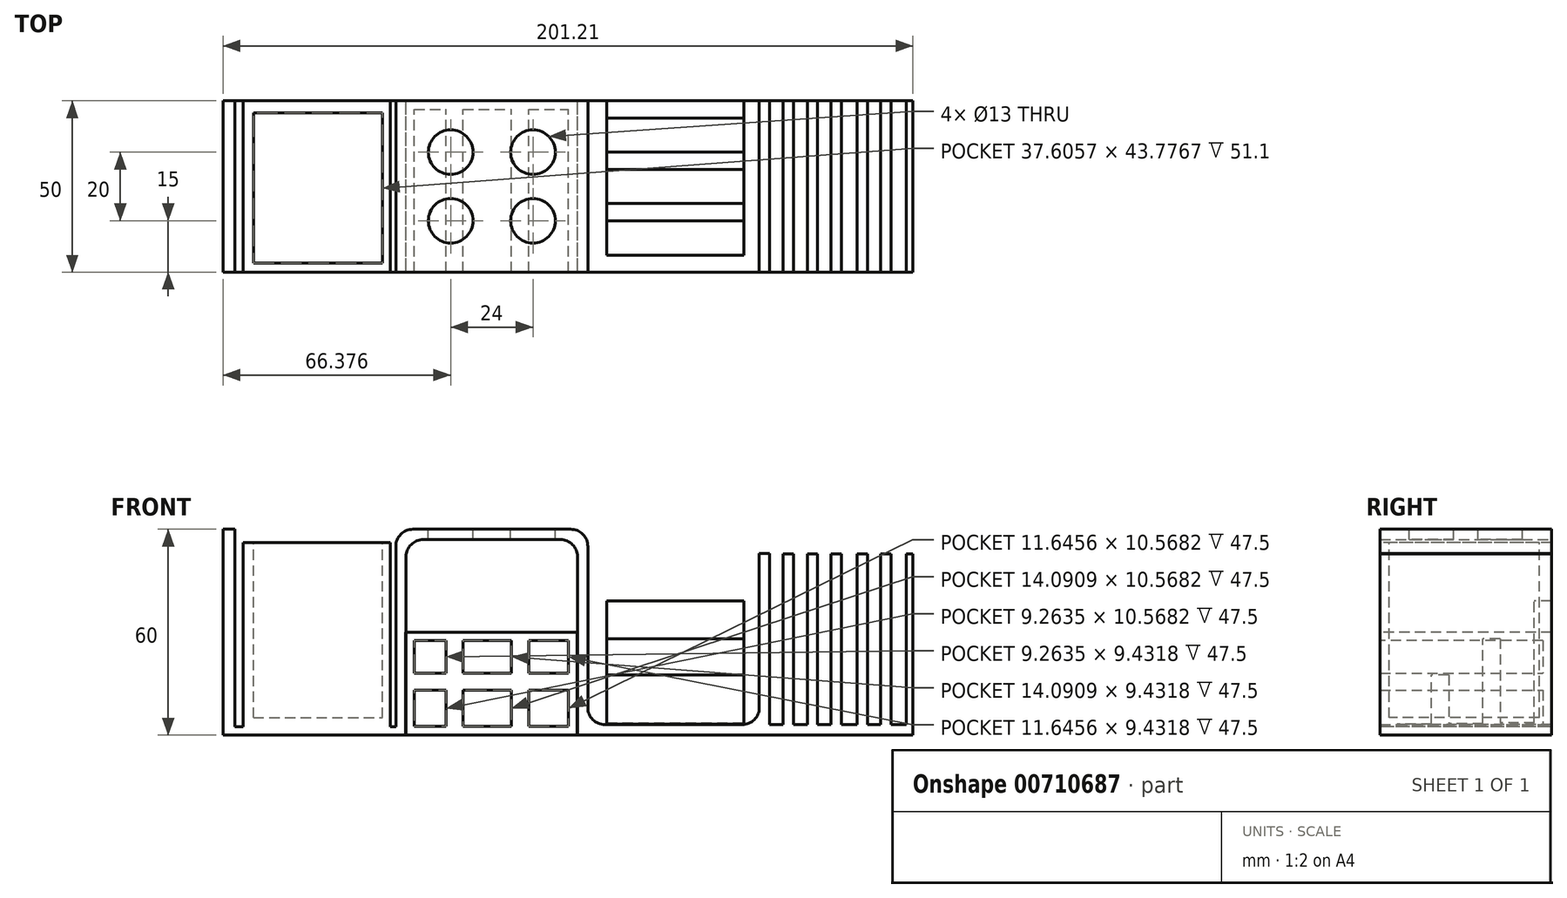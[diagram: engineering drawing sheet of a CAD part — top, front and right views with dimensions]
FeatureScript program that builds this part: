
annotation { "Feature Type Name" : "Feature", "Feature Type Description" : "" }
export const myFeature = defineFeature(function(context is Context, id is Id, definition is map)
    precondition{}
    {
        {
            var Q0;
            Q0=qCreatedBy(makeId("Front.planeOp"),FACE);
            var sketch = newSketch(context, id + "F0", { "sketchPlane" : qUnion([Q0])});
            skLineSegment(sketch, "E0.top", {"start": v(4.58, 57) * mm, "end": v(54.58, 57) * mm});
            skLineSegment(sketch, "E0.left", {"start": v(4.58, 0) * mm, "end": v(4.58, 57) * mm});
            skLineSegment(sketch, "E0.right", {"start": v(54.58, 0) * mm, "end": v(54.58, 57) * mm});
            skLineSegment(sketch, "E1.top", {"start": v(57.58, 3) * mm, "end": v(107.58, 3) * mm});
            skLineSegment(sketch, "E1.left", {"start": v(57.58, 60) * mm, "end": v(57.58, 3) * mm});
            skLineSegment(sketch, "E1.right", {"start": v(107.58, 53) * mm, "end": v(107.58, 3) * mm});
            skLineSegment(sketch, "E2", {"start": v(1.58, 0) * mm, "end": v(4.58, 0) * mm});
            skLineSegment(sketch, "E3", {"start": v(54.58, 0) * mm, "end": v(110.58, 0) * mm});
            skLineSegment(sketch, "E4", {"start": v(1.58, 60) * mm, "end": v(57.58, 60) * mm});
            skLineSegment(sketch, "E5", {"start": v(110.58, 53) * mm, "end": v(107.58, 53) * mm});
            skLineSegment(sketch, "E6.bottom", {"start": v(1.58, 0) * mm, "end": v(-45.36, 0) * mm});
            skLineSegment(sketch, "E6.top", {"start": v(1.58, 2.45) * mm, "end": v(-45.36, 2.45) * mm});
            skLineSegment(sketch, "E7.bottom", {"start": v(-45.36, 0) * mm, "end": v(-48.8, 0) * mm});
            skLineSegment(sketch, "E7.top", {"start": v(-45.36, 60) * mm, "end": v(-48.8, 60) * mm});
            skLineSegment(sketch, "E7.right", {"start": v(-48.8, 0) * mm, "end": v(-48.8, 60) * mm});
            skLineSegment(sketch, "E8", {"start": v(-45.36, 60) * mm, "end": v(-45.36, 2.45) * mm});
            skLineSegment(sketch, "E9", {"start": v(1.58, 60) * mm, "end": v(1.58, 2.45) * mm});
            skLineSegment(sketch, "E10.bottom", {"start": v(110.58, 0) * mm, "end": v(152.41, 0) * mm});
            skLineSegment(sketch, "E10.top", {"start": v(110.58, 3.01) * mm, "end": v(152.41, 3.01) * mm});
            skLineSegment(sketch, "E10.right", {"start": v(152.41, 0) * mm, "end": v(152.41, 3.01) * mm});
            skLineSegment(sketch, "E11", {"start": v(110.58, 53) * mm, "end": v(110.58, 3.01) * mm});
            skLineSegment(sketch, "E12.bottom", {"start": v(114.5, 3.01) * mm, "end": v(117.5, 3.01) * mm});
            skLineSegment(sketch, "E12.top", {"start": v(114.5, 52.83) * mm, "end": v(117.5, 52.83) * mm});
            skLineSegment(sketch, "E12.left", {"start": v(114.5, 3.01) * mm, "end": v(114.5, 52.83) * mm});
            skLineSegment(sketch, "E12.right", {"start": v(117.5, 3.01) * mm, "end": v(117.5, 52.83) * mm});
            skLineSegment(sketch, "E13.bottom", {"start": v(121.6, 3.01) * mm, "end": v(124.6, 3.01) * mm});
            skLineSegment(sketch, "E13.top", {"start": v(121.6, 52.83) * mm, "end": v(124.6, 52.83) * mm});
            skLineSegment(sketch, "E13.left", {"start": v(121.6, 3.01) * mm, "end": v(121.6, 52.83) * mm});
            skLineSegment(sketch, "E13.right", {"start": v(124.6, 3.01) * mm, "end": v(124.6, 52.83) * mm});
            skLineSegment(sketch, "E14.bottom", {"start": v(128.48, 3.01) * mm, "end": v(131.48, 3.01) * mm});
            skLineSegment(sketch, "E14.top", {"start": v(128.48, 52.83) * mm, "end": v(131.48, 52.83) * mm});
            skLineSegment(sketch, "E14.left", {"start": v(128.48, 3.01) * mm, "end": v(128.48, 52.83) * mm});
            skLineSegment(sketch, "E14.right", {"start": v(131.48, 3.01) * mm, "end": v(131.48, 52.83) * mm});
            skLineSegment(sketch, "E15.bottom", {"start": v(136.1, 3.01) * mm, "end": v(139.1, 3.01) * mm});
            skLineSegment(sketch, "E15.top", {"start": v(136.1, 52.83) * mm, "end": v(139.1, 52.83) * mm});
            skLineSegment(sketch, "E15.left", {"start": v(136.1, 3.01) * mm, "end": v(136.1, 52.83) * mm});
            skLineSegment(sketch, "E15.right", {"start": v(139.1, 3.01) * mm, "end": v(139.1, 52.83) * mm});
            skLineSegment(sketch, "E16.bottom", {"start": v(142.98, 3.01) * mm, "end": v(145.98, 3.01) * mm});
            skLineSegment(sketch, "E16.top", {"start": v(142.98, 52.83) * mm, "end": v(145.98, 52.83) * mm});
            skLineSegment(sketch, "E16.left", {"start": v(142.98, 3.01) * mm, "end": v(142.98, 52.83) * mm});
            skLineSegment(sketch, "E16.right", {"start": v(145.98, 3.01) * mm, "end": v(145.98, 52.83) * mm});
            skLineSegment(sketch, "E17.bottom", {"start": v(152.41, 3.01) * mm, "end": v(150.41, 3.01) * mm});
            skLineSegment(sketch, "E17.top", {"start": v(152.41, 52.83) * mm, "end": v(150.41, 52.83) * mm});
            skLineSegment(sketch, "E17.left", {"start": v(152.41, 3.01) * mm, "end": v(152.41, 52.83) * mm});
            skLineSegment(sketch, "E17.right", {"start": v(150.41, 3.01) * mm, "end": v(150.41, 52.83) * mm});
            skLineSegment(sketch, "E18", {"start": v(107.58, 3) * mm, "end": v(107.58, 0) * mm});
            skSolve(sketch);
        }
        {
            var Q0;
            Q0=qSketchRegion(id+"F0",true);
            extrude(context, id + "F1", {"entities" : qUnion([Q0]), "depth" : 50 * mm, "offsetDistance" : 25 * mm});
        }
        {
            var Q0;
            Q0=makeQuery(id+"F1.opExtrude","SWEPT_FACE",FACE,{"disambiguationData":[OSD([sQuery(id+"F0.wireOp",EDGE,"E4")])]});
            var sketch = newSketch(context, id + "F2", { "sketchPlane" : qUnion([Q0])});
            skCircle(sketch, "E19", {"center": v(17.58, -15) * mm, "radius": 6.5 * mm});
            skCircle(sketch, "E20", {"center": v(41.58, -15) * mm, "radius": 6.5 * mm});
            skCircle(sketch, "E21", {"center": v(17.58, -35) * mm, "radius": 6.5 * mm});
            skCircle(sketch, "E22", {"center": v(41.58, -35) * mm, "radius": 6.5 * mm});
            skSolve(sketch);
        }
        {
            var Q0;
            Q0=qCreatedBy(makeId("Top.planeOp"),FACE);
            var sketch = newSketch(context, id + "F3", { "sketchPlane" : qUnion([Q0])});
            skLineSegment(sketch, "E23.bottom", {"start": v(4.44, 0) * mm, "end": v(54.44, 0) * mm});
            skLineSegment(sketch, "E23.top", {"start": v(4.44, -50) * mm, "end": v(54.44, -50) * mm});
            skLineSegment(sketch, "E23.left", {"start": v(4.44, 0) * mm, "end": v(4.44, -50) * mm});
            skLineSegment(sketch, "E23.right", {"start": v(54.44, 0) * mm, "end": v(54.44, -50) * mm});
            skSolve(sketch);
        }
        {
            var Q0;
            Q0=makeQuery(id+"F1.opExtrude","SWEPT_FACE",FACE,{"disambiguationData":[OSD([sQuery(id+"F0.wireOp",EDGE,"E1.top")])]});
            var sketch = newSketch(context, id + "F4", { "sketchPlane" : qUnion([Q0])});
            skLineSegment(sketch, "E24.bottom", {"start": v(63.1, 0) * mm, "end": v(103.1, 0) * mm});
            skLineSegment(sketch, "E24.top", {"start": v(63.1, -15) * mm, "end": v(103.1, -15) * mm});
            skLineSegment(sketch, "E24.left", {"start": v(63.1, 0) * mm, "end": v(63.1, -15) * mm});
            skLineSegment(sketch, "E24.right", {"start": v(103.1, 0) * mm, "end": v(103.1, -15) * mm});
            skSolve(sketch);
        }
        {
            var Q0;
            Q0=qSketchRegion(id+"F4",true);
            extrude(context, id + "F5", {"entities" : qUnion([Q0]), "operationType" : NewBodyOperationType.ADD, "depth" : 36.1 * mm});
        }
        {
            var Q0;
            Q0=makeQuery(id+"F5.opExtrude","CAP_FACE",FACE,{"disambiguationData":[OSD([sQuery(id+"F4.wireOp",EDGE,"E24.bottom"),sQuery(id+"F4.wireOp",EDGE,"E24.top"),sQuery(id+"F4.wireOp",EDGE,"E24.left"),sQuery(id+"F4.wireOp",EDGE,"E24.right")])],"isStart":false});
            var sketch = newSketch(context, id + "F6", { "sketchPlane" : qUnion([Q0])});
            skLineSegment(sketch, "E25.bottom", {"start": v(63.1, -15) * mm, "end": v(103.1, -15) * mm});
            skLineSegment(sketch, "E25.top", {"start": v(63.1, -5) * mm, "end": v(103.1, -5) * mm});
            skLineSegment(sketch, "E25.left", {"start": v(63.1, -15) * mm, "end": v(63.1, -5) * mm});
            skLineSegment(sketch, "E25.right", {"start": v(103.1, -15) * mm, "end": v(103.1, -5) * mm});
            skSolve(sketch);
        }
        {
            var Q0;
            Q0=qSketchRegion(id+"F6",true);
            extrude(context, id + "F7", {"entities" : qUnion([Q0]), "operationType" : NewBodyOperationType.REMOVE, "oppositeDirection" : true, "depth" : 35.5 * mm});
        }
        {
            var Q0;
            Q0=makeQuery(id+"F1.opExtrude","SWEPT_FACE",FACE,{"disambiguationData":[OSD([sQuery(id+"F0.wireOp",EDGE,"E1.top")])]});
            var sketch = newSketch(context, id + "F8", { "sketchPlane" : qUnion([Q0])});
            skLineSegment(sketch, "E26.bottom", {"start": v(63.1, -15) * mm, "end": v(103.1, -15) * mm});
            skLineSegment(sketch, "E26.top", {"start": v(63.1, -30) * mm, "end": v(103.1, -30) * mm});
            skLineSegment(sketch, "E26.left", {"start": v(63.1, -15) * mm, "end": v(63.1, -30) * mm});
            skLineSegment(sketch, "E26.right", {"start": v(103.1, -15) * mm, "end": v(103.1, -30) * mm});
            skSolve(sketch);
        }
        {
            var Q0;
            Q0=qSketchRegion(id+"F8",true);
            extrude(context, id + "F9", {"entities" : qUnion([Q0]), "operationType" : NewBodyOperationType.ADD, "depth" : 25.1 * mm});
        }
        {
            var Q0;
            Q0=makeQuery(id+"F9.opExtrude","CAP_FACE",FACE,{"disambiguationData":[OSD([sQuery(id+"F8.wireOp",EDGE,"E26.bottom"),sQuery(id+"F8.wireOp",EDGE,"E26.top"),sQuery(id+"F8.wireOp",EDGE,"E26.left"),sQuery(id+"F8.wireOp",EDGE,"E26.right")])],"isStart":false});
            var sketch = newSketch(context, id + "F10", { "sketchPlane" : qUnion([Q0])});
            skLineSegment(sketch, "E27.bottom", {"start": v(63.1, -30) * mm, "end": v(103.1, -30) * mm});
            skLineSegment(sketch, "E27.top", {"start": v(63.1, -20) * mm, "end": v(103.1, -20) * mm});
            skLineSegment(sketch, "E27.left", {"start": v(63.1, -30) * mm, "end": v(63.1, -20) * mm});
            skLineSegment(sketch, "E27.right", {"start": v(103.1, -30) * mm, "end": v(103.1, -20) * mm});
            skSolve(sketch);
        }
        {
            var Q0;
            Q0=qSketchRegion(id+"F10",true);
            extrude(context, id + "F11", {"entities" : qUnion([Q0]), "operationType" : NewBodyOperationType.REMOVE, "oppositeDirection" : true, "depth" : 24.8 * mm});
        }
        {
            var Q0;
            Q0=makeQuery(id+"F1.opExtrude","SWEPT_FACE",FACE,{"disambiguationData":[OSD([sQuery(id+"F0.wireOp",EDGE,"E1.top")])]});
            var sketch = newSketch(context, id + "F12", { "sketchPlane" : qUnion([Q0])});
            skLineSegment(sketch, "E28.bottom", {"start": v(63.1, -30) * mm, "end": v(103.1, -30) * mm});
            skLineSegment(sketch, "E28.top", {"start": v(63.1, -45) * mm, "end": v(103.1, -45) * mm});
            skLineSegment(sketch, "E28.left", {"start": v(63.1, -30) * mm, "end": v(63.1, -45) * mm});
            skLineSegment(sketch, "E28.right", {"start": v(103.1, -30) * mm, "end": v(103.1, -45) * mm});
            skSolve(sketch);
        }
        {
            var Q0;
            Q0=qSketchRegion(id+"F12",true);
            extrude(context, id + "F13", {"entities" : qUnion([Q0]), "operationType" : NewBodyOperationType.ADD, "depth" : 14.5 * mm});
        }
        {
            var Q0;
            Q0=makeQuery(id+"F13.opExtrude","CAP_FACE",FACE,{"disambiguationData":[OSD([sQuery(id+"F12.wireOp",EDGE,"E28.bottom"),sQuery(id+"F12.wireOp",EDGE,"E28.top"),sQuery(id+"F12.wireOp",EDGE,"E28.left"),sQuery(id+"F12.wireOp",EDGE,"E28.right")])],"isStart":false});
            var sketch = newSketch(context, id + "F14", { "sketchPlane" : qUnion([Q0])});
            skLineSegment(sketch, "E29.bottom", {"start": v(63.1, -45) * mm, "end": v(103.1, -45) * mm});
            skLineSegment(sketch, "E29.top", {"start": v(63.1, -35) * mm, "end": v(103.1, -35) * mm});
            skLineSegment(sketch, "E29.left", {"start": v(63.1, -45) * mm, "end": v(63.1, -35) * mm});
            skLineSegment(sketch, "E29.right", {"start": v(103.1, -45) * mm, "end": v(103.1, -35) * mm});
            skSolve(sketch);
        }
        {
            var Q0;
            Q0=qSketchRegion(id+"F14",true);
            extrude(context, id + "F15", {"entities" : qUnion([Q0]), "operationType" : NewBodyOperationType.REMOVE, "oppositeDirection" : true, "depth" : 14.3 * mm});
        }
        {
            var Q0;
            Q0=makeQuery(id+"F1.opExtrude","SWEPT_EDGE",EDGE,{"disambiguationData":[OSD([sQuery(id+"F0.wireOp",EDGE,"E1.left"),sQuery(id+"F0.wireOp",EDGE,"E4")])]});
            var Q1;
            Q1=makeQuery(id+"F1.opExtrude","SWEPT_EDGE",EDGE,{"disambiguationData":[OSD([sQuery(id+"F0.wireOp",EDGE,"E0.top"),sQuery(id+"F0.wireOp",EDGE,"E0.right")])]});
            var Q2;
            Q2=makeQuery(id+"F1.opExtrude","SWEPT_EDGE",EDGE,{"disambiguationData":[OSD([sQuery(id+"F0.wireOp",EDGE,"xXto4Pc0-SdtI-9WrI-qXPa-qfZvLXBMMGb8.left"),sQuery(id+"F0.wireOp",EDGE,"E4")])]});
            var Q3;
            Q3=makeQuery(id+"F1.opExtrude","SWEPT_EDGE",EDGE,{"disambiguationData":[OSD([sQuery(id+"F0.wireOp",EDGE,"E0.top"),sQuery(id+"F0.wireOp",EDGE,"E0.left")])]});
            var Q4;
            Q4=makeQuery(id+"F1.opExtrude","SWEPT_EDGE",EDGE,{"disambiguationData":[OSD([sQuery(id+"F0.wireOp",EDGE,"E1.top"),sQuery(id+"F0.wireOp",EDGE,"E1.left")])]});
            var Q5;
            Q5=makeQuery(id+"F1.opExtrude","SWEPT_EDGE",EDGE,{"disambiguationData":[OSD([sQuery(id+"F0.wireOp",EDGE,"E1.top"),sQuery(id+"F0.wireOp",EDGE,"E1.right")])]});
            fillet(context, id + "F16", {"entities" : qUnion([Q0, Q1, Q2, Q3, Q4, Q5]), "radius" : 5 * mm, "tangentPropagation" : true, "allowEdgeOverflow" : false});
        }
        {
            var Q0;
            Q0=qSketchRegion(id+"F3",true);
            extrude(context, id + "F17", {"entities" : qUnion([Q0]), "depth" : 30 * mm});
        }
        {
            var Q0;
            Q0=makeQuery(id+"F17.opExtrude","SWEPT_FACE",FACE,{"disambiguationData":[OSD([sQuery(id+"F3.wireOp",EDGE,"E23.top")])]});
            shell(context, id + "F18", {"entities" : qUnion([Q0]), "thickness" : 2.5 * mm});
        }
        {
            var Q0;
            Q0=qSketchRegion(id+"F2",true);
            var Q1;
            Q1=qSketchRegion(id+"F10",true);
            extrude(context, id + "F19", {"entities" : qUnion([Q0, Q1]), "operationType" : NewBodyOperationType.REMOVE, "oppositeDirection" : true, "depth" : 13.9 * mm});
        }
        {
            var Q0;
            Q0=makeQuery(id+"F1.opExtrude","SWEPT_FACE",FACE,{"disambiguationData":[OSD([sQuery(id+"F0.wireOp",EDGE,"E6.top")])]});
            var sketch = newSketch(context, id + "F20", { "sketchPlane" : qUnion([Q0])});
            skLineSegment(sketch, "E30.bottom", {"start": v(-43, 0) * mm, "end": v(0, 0) * mm});
            skLineSegment(sketch, "E30.top", {"start": v(-43, -50) * mm, "end": v(0, -50) * mm});
            skLineSegment(sketch, "E30.left", {"start": v(-43, 0) * mm, "end": v(-43, -50) * mm});
            skLineSegment(sketch, "E30.right", {"start": v(0, 0) * mm, "end": v(0, -50) * mm});
            skSolve(sketch);
        }
        {
            var Q0;
            Q0=qSketchRegion(id+"F20",true);
            extrude(context, id + "F21", {"entities" : qUnion([Q0]), "operationType" : NewBodyOperationType.ADD, "depth" : 53.7 * mm});
        }
        {
            var Q0;
            Q0=makeQuery(id+"F21.opExtrude","CAP_FACE",FACE,{"disambiguationData":[OSD([sQuery(id+"F20.wireOp",EDGE,"E30.bottom"),sQuery(id+"F20.wireOp",EDGE,"E30.top"),sQuery(id+"F20.wireOp",EDGE,"E30.left"),sQuery(id+"F20.wireOp",EDGE,"E30.right")])],"isStart":false});
            var sketch = newSketch(context, id + "F22", { "sketchPlane" : qUnion([Q0])});
            skLineSegment(sketch, "E31.bottom", {"start": v(-39.95, -3.55) * mm, "end": v(-2.35, -3.55) * mm});
            skLineSegment(sketch, "E31.top", {"start": v(-39.95, -47.33) * mm, "end": v(-2.35, -47.33) * mm});
            skLineSegment(sketch, "E31.left", {"start": v(-39.95, -3.55) * mm, "end": v(-39.95, -47.33) * mm});
            skLineSegment(sketch, "E31.right", {"start": v(-2.35, -3.55) * mm, "end": v(-2.35, -47.33) * mm});
            skSolve(sketch);
        }
        {
            var Q0;
            Q0=qSketchRegion(id+"F22",true);
            extrude(context, id + "F23", {"entities" : qUnion([Q0]), "operationType" : NewBodyOperationType.REMOVE, "oppositeDirection" : true, "depth" : 51.1 * mm});
        }
        {
            var Q0;
            Q0=makeQuery(id+"F18.opShell","OFFSET_FACE",FACE,{"disambiguationData":[OSD([sQuery(id+"F3.wireOp",EDGE,"E23.bottom")])]});
            var sketch = newSketch(context, id + "F24", { "sketchPlane" : qUnion([Q0])});
            skLineSegment(sketch, "E32.bottom", {"start": v(6.94, 18.07) * mm, "end": v(51.94, 18.07) * mm});
            skLineSegment(sketch, "E32.top", {"start": v(6.94, 13.07) * mm, "end": v(51.94, 13.07) * mm});
            skLineSegment(sketch, "E32.left", {"start": v(6.94, 18.07) * mm, "end": v(6.94, 13.07) * mm});
            skLineSegment(sketch, "E32.right", {"start": v(51.94, 18.07) * mm, "end": v(51.94, 13.07) * mm});
            skLineSegment(sketch, "E33.bottom", {"start": v(16.2, 27.5) * mm, "end": v(21.2, 27.5) * mm});
            skLineSegment(sketch, "E33.top", {"start": v(16.2, 2.5) * mm, "end": v(21.2, 2.5) * mm});
            skLineSegment(sketch, "E33.left", {"start": v(16.2, 27.5) * mm, "end": v(16.2, 2.5) * mm});
            skLineSegment(sketch, "E33.right", {"start": v(21.2, 27.5) * mm, "end": v(21.2, 2.5) * mm});
            skLineSegment(sketch, "E34.bottom", {"start": v(35.3, 27.5) * mm, "end": v(40.3, 27.5) * mm});
            skLineSegment(sketch, "E34.top", {"start": v(35.3, 2.5) * mm, "end": v(40.3, 2.5) * mm});
            skLineSegment(sketch, "E34.left", {"start": v(35.3, 27.5) * mm, "end": v(35.3, 2.5) * mm});
            skLineSegment(sketch, "E34.right", {"start": v(40.3, 27.5) * mm, "end": v(40.3, 2.5) * mm});
            skSolve(sketch);
        }
        {
            var Q0;
            Q0=qSketchRegion(id+"F24",true);
            extrude(context, id + "F25", {"entities" : qUnion([Q0]), "operationType" : NewBodyOperationType.ADD, "depth" : 47.5 * mm});
        }
    });
